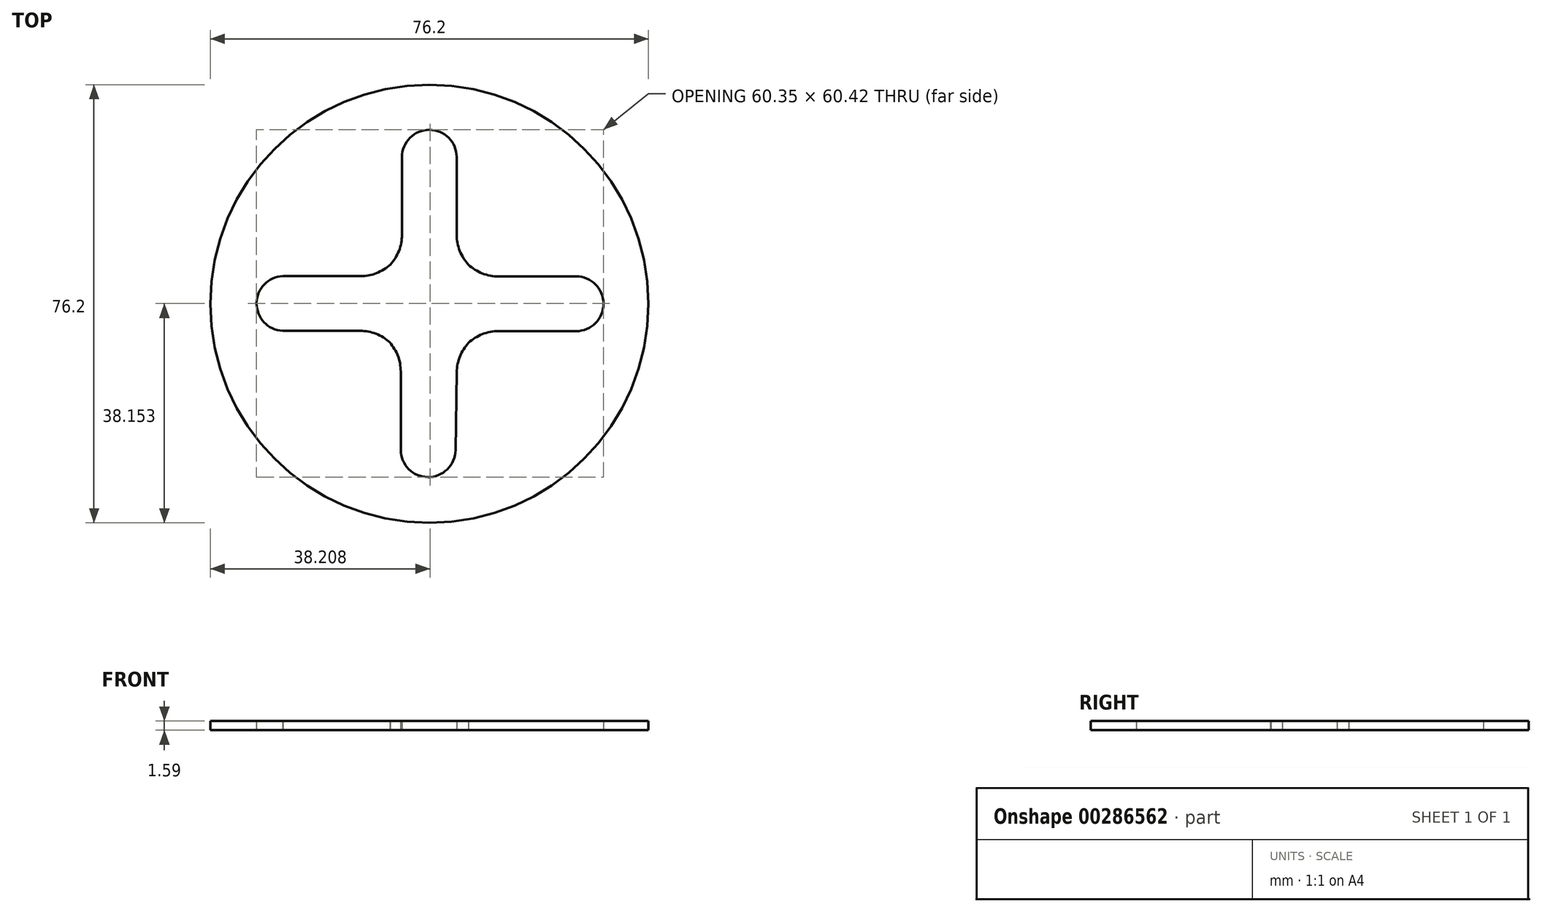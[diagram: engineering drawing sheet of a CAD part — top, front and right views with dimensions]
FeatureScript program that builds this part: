
annotation { "Feature Type Name" : "Feature", "Feature Type Description" : "" }
export const myFeature = defineFeature(function(context is Context, id is Id, definition is map)
    precondition{}
    {
        {
            var Q0;
            Q0=qCreatedBy(makeId("Top.planeOp"),FACE);
            var sketch = newSketch(context, id + "F0", { "sketchPlane" : qUnion([Q0])});
            skCircle(sketch, "E0", {"center": v(0, 0) * mm, "radius": 38.1 * mm});
            skArc(sketch, "E1", {"start": v(25.52, -4.76) * mm, "mid": v(30.28, 0) * mm, "end": v(25.52, 4.77) * mm});
            skLineSegment(sketch, "E2", {"start": v(25.52, 4.77) * mm, "end": v(8.37, 4.76) * mm});
            skLineSegment(sketch, "E3", {"start": v(8.37, -4.76) * mm, "end": v(25.52, -4.76) * mm});
            skLineSegment(sketch, "E4.MirrorCS", {"start": v(-4.98, -25.4) * mm, "end": v(-4.98, -8.24) * mm});
            skLineSegment(sketch, "E5.MirrorCS", {"start": v(4.76, 8.37) * mm, "end": v(4.76, 25.52) * mm});
            skLineSegment(sketch, "E6.MirrorCS", {"start": v(-4.77, 25.52) * mm, "end": v(-4.77, 8.36) * mm});
            skLineSegment(sketch, "E7.MirrorCS", {"start": v(-8.4, -4.7) * mm, "end": v(-25.56, -4.7) * mm});
            skLineSegment(sketch, "E8.MirrorCS", {"start": v(-25.49, 4.82) * mm, "end": v(-8.34, 4.82) * mm});
            skLineSegment(sketch, "E9.MirrorCS", {"start": v(4.81, -8.34) * mm, "end": v(4.54, -25.49) * mm});
            skArc(sketch, "E10.MirrorCS", {"start": v(4.76, 25.52) * mm, "mid": v(-0.01, 30.26) * mm, "end": v(-4.77, 25.52) * mm});
            skArc(sketch, "E11.MirrorCS", {"start": v(-25.56, -4.7) * mm, "mid": v(-30.07, 0.1) * mm, "end": v(-25.49, 4.82) * mm});
            skArc(sketch, "E12.MirrorCS", {"start": v(4.54, -25.49) * mm, "mid": v(-0.26, -30.16) * mm, "end": v(-4.98, -25.4) * mm});
            skArc(sketch, "E13", {"start": v(-8.4, -4.7) * mm, "mid": v(-6.92, -6.7) * mm, "end": v(-4.98, -8.24) * mm});
            skArc(sketch, "E14", {"start": v(-4.77, 8.36) * mm, "mid": v(-6.79, 6.83) * mm, "end": v(-8.34, 4.82) * mm});
            skArc(sketch, "E15.trimOffspring", {"start": v(8.37, 4.76) * mm, "mid": v(6.8, 6.8) * mm, "end": v(4.76, 8.37) * mm});
            skArc(sketch, "E16.trimOffspring", {"start": v(4.81, -8.34) * mm, "mid": v(6.83, -6.79) * mm, "end": v(8.37, -4.76) * mm});
            skSolve(sketch);
        }
        {
            var Q0;
            Q0=qSketchRegion(id+"F0",true);
            extrude(context, id + "F1", {"entities" : qUnion([Q0]), "depth" : 1.59 * mm});
        }
        {
            var Q0;
            Q0=makeQuery(id+"F1.opExtrude","SWEPT_EDGE",EDGE,{"disambiguationData":[OSD([sQuery(id+"F0.wireOp",EDGE,"E8.MirrorCS"),sQuery(id+"F0.wireOp",EDGE,"E14")])]});
            var Q1;
            Q1=makeQuery(id+"F1.opExtrude","SWEPT_EDGE",EDGE,{"disambiguationData":[OSD([sQuery(id+"F0.wireOp",EDGE,"E6.MirrorCS"),sQuery(id+"F0.wireOp",EDGE,"E14")])]});
            var Q2;
            Q2=makeQuery(id+"F1.opExtrude","SWEPT_EDGE",EDGE,{"disambiguationData":[OSD([sQuery(id+"F0.wireOp",EDGE,"E5.MirrorCS"),sQuery(id+"F0.wireOp",EDGE,"E15.trimOffspring")])]});
            var Q3;
            Q3=makeQuery(id+"F1.opExtrude","SWEPT_EDGE",EDGE,{"disambiguationData":[OSD([sQuery(id+"F0.wireOp",EDGE,"E2"),sQuery(id+"F0.wireOp",EDGE,"E15.trimOffspring")])]});
            var Q4;
            Q4=makeQuery(id+"F1.opExtrude","SWEPT_EDGE",EDGE,{"disambiguationData":[OSD([sQuery(id+"F0.wireOp",EDGE,"E3"),sQuery(id+"F0.wireOp",EDGE,"E16.trimOffspring")])]});
            var Q5;
            Q5=makeQuery(id+"F1.opExtrude","SWEPT_EDGE",EDGE,{"disambiguationData":[OSD([sQuery(id+"F0.wireOp",EDGE,"E9.MirrorCS"),sQuery(id+"F0.wireOp",EDGE,"E16.trimOffspring")])]});
            var Q6;
            Q6=makeQuery(id+"F1.opExtrude","SWEPT_EDGE",EDGE,{"disambiguationData":[OSD([sQuery(id+"F0.wireOp",EDGE,"E4.MirrorCS"),sQuery(id+"F0.wireOp",EDGE,"E13")])]});
            var Q7;
            Q7=makeQuery(id+"F1.opExtrude","SWEPT_EDGE",EDGE,{"disambiguationData":[OSD([sQuery(id+"F0.wireOp",EDGE,"E7.MirrorCS"),sQuery(id+"F0.wireOp",EDGE,"E13")])]});
            fillet(context, id + "F2", {"entities" : qUnion([Q0, Q1, Q2, Q3, Q4, Q5, Q6, Q7]), "radius" : 7.62 * mm, "tangentPropagation" : true, "allowEdgeOverflow" : false});
        }
    });
